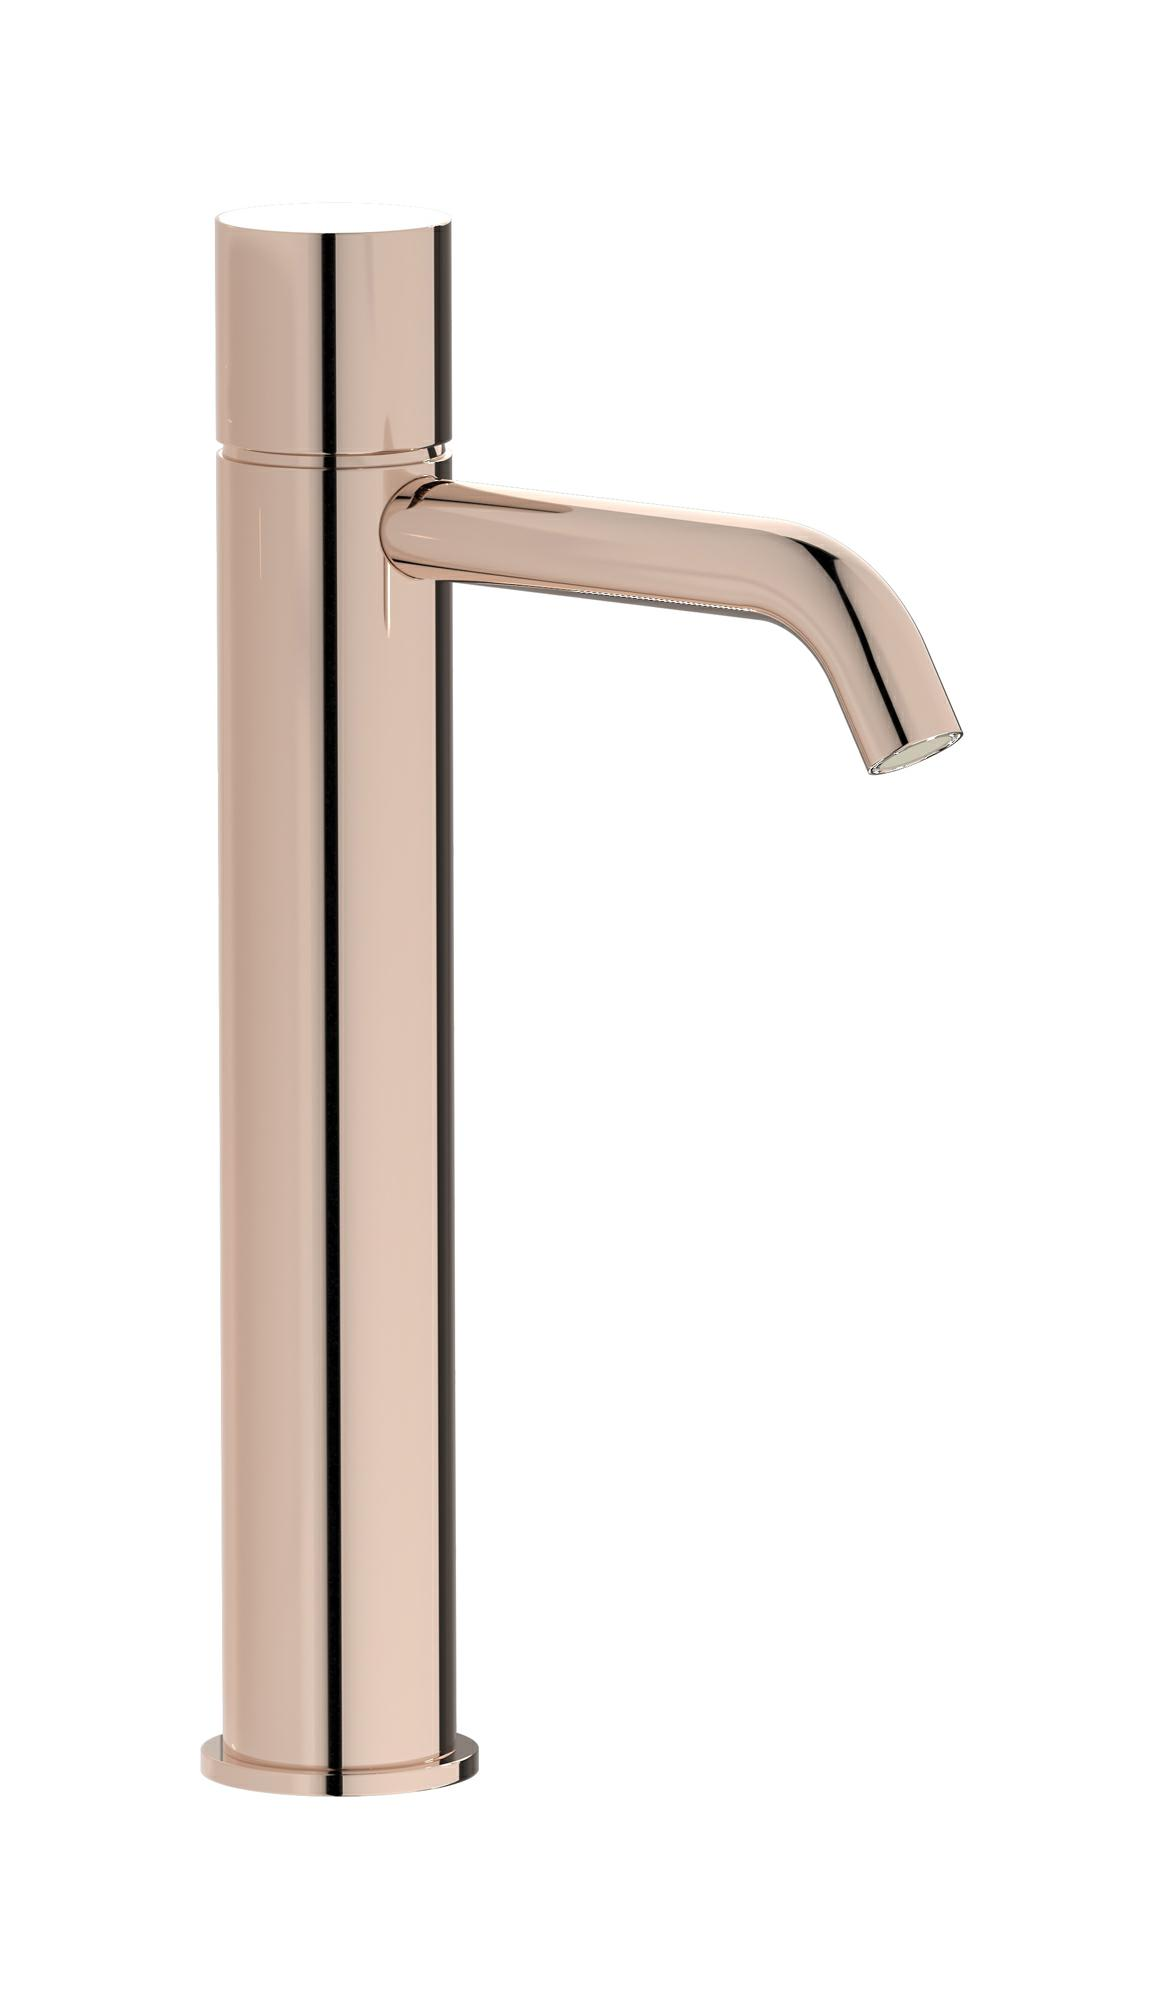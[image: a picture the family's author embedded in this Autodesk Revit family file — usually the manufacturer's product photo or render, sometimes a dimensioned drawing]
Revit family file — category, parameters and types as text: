
# Revit family: RR202
name_source: partatom
category: Apparecchi idraulici
units: mm (PartAtom-declared; Revit-internal decimal feet)

## family parameters
Basato su piano di lavoro = No
Condiviso = No
Mantieni orientamento annotazione = No
Numero OmniClass = 23.45.55.17
Punto di calcolo locali = No
Quota connettore circolare = Usa diametro
Sempre verticale = Sì
Taglio con vuoti quando caricato = No
Tipo di parte = Normale
Titolo OmniClass = Mixing Faucets

## types (13) — shared parameters
Cold water inlet = 10 mm  [stored 0.0328084 ft]
Commenti sul tipo = Tall monohole washbasin mixer complete with drain
Connessione CW = No
Connessione HW = No
Connessione di scarico = No
Connessione di ventilazione = No
Descrizione = Tall monohole washbasin mixer complete with drain
Hot water inlet = 10 mm  [stored 0.0328084 ft]
Produttore = IB Rubinetterie S.p.A.
URL = https://www.weareib.it
zero-valued in all types: Prospetto di default

## per-type parameters (varying)
| type | Finishes surface | Immagine tipo | Modello |
| Chrome | IB_Chrome | RR202CC.jpg | RR202CC |
| Matt White | IB_matt white | RR202BO.jpg | RR202BO |
| Black Chrome | IB_Black chrome | RR202CF.jpg | RR202CF |
| Brushed Black Chrome | IB_Brushed black chrome | RR202CS.jpg | RR202CS |
| Pale Gold | IB_Pale gold | RR202II.jpg | RR202II |
| Brushed Pale Gold | IB_brushed pale gold | RR202IS.jpg | RR202IS |
| Modern Bronze | IB_Modern bronze | RR202MB.jpg | RR202MB |
| Matt Black | IB_matt black | RR202NP.jpg | RR202NP |
| Gold | IB_gold | RR202OO.jpg | RR202OO |
| Brushed Gold | IB_brushed gold | RR202OS.jpg | RR202OS |
| Rose Gold | IB_Rose gold | RR202RS.jpg | RR202RS |
| Brushed Rose Gold | IB_Brushed rose gold | RR202SR.jpg | RR202SR |
| Brushed Nickel | IB_Brushed nickel | RR202SS.jpg | RR202SS |

note: [stored X ft] marks values corroborated as IEEE doubles in the binary element streams (Revit-internal decimal feet)
